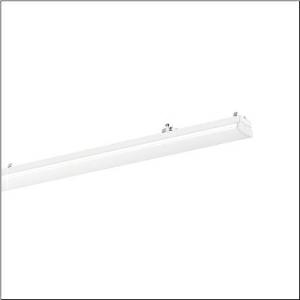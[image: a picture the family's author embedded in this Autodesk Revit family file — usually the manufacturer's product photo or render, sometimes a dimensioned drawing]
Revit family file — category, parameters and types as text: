
# Revit family: licross_r__11_recessed_opal_ho_51tl1dcn4cxm_8f08
name_source: partatom
category: Lighting Fixtures
units: mm (PartAtom-declared; Revit-internal decimal feet)

## family parameters
Cut with Voids When Loaded = No
Host = Face
Light Source = No
Part Type = Normal
Room Calculation Point = No
Round Connector Dimension = Use Diameter
Shared = No

## types (1)
- --- (1 x LED, 12370 lm, 66.5 W, 4000K)
    Apparent Load = 67 VA
    CIE Flux Codes = 44 73 91 87 100
    Color Rendering = 80
    Color Temperature = 4000K
    Default Elevation = 1800 mm
    Description = Licross® 11 recessed opal HO, luminaire insert, of sheet steel, coil coated, white, length: 1.500mm, width: 76mm, height: 87mm, LED rated luminous flux: 12.370lm, light colour: 840, control gear: ON/OFF Multilumen, CLOi, with plug, 3-pole, with phase selection, mains connection: 220..240V, AC, 50/60Hz, start of lifetime: 67W, end of service life: 75W, internal wiring halogen-free, primary optical cover: cover, of PMMA, light emission: direct with ceiling illumination distribution, primary light characteristic: symmetric, protection rating (complete): IP40, insulation class (complete): insulation class I (protective earthing), certification: CE, ENEC, VDE, UKCA, protection symbol: D if used in an environment without relevant dust loads with corresponding accessories, impact resistance: IK06, permissible ambient temperature for indoor applications: -35..+35°C, corresponds to IFS (International Featured Standards) requirements for safety and quality in the food industry, reducing of maximum allowable ambient temperature of 5°C with ceiling mounting, LABS conformity tested according to VDMA 24364:2018-05, packaging unit: 1 piece
    Height = 83 mm
    Lamp = 1 x LED
    Lamp Light Flux = 12370 lm
    Lamp Power = 66.5 W
    Lamp count = 1
    Length = 1500 mm
    Luminous efficacy = 186 lm/W
    Manufacturer = Siteco
    ModVariant = No
    Model = 51TL1DCN4CXM
    Mounting Place = Ceiling
    Mounting Type = Pendant
    Number of Poles = 1
    OnlyDefault = Yes
    Power Factor = 1
    Product Name = Licross® 11 recessed opal HO
    Product group = luminaire insert | ceiling pendant
    ProductGroupID = 902
    Protection Class = Protection class I
    Protection Degree = IP 40
    RLX_Detail_Level = 1
    RLX_Emergency_Light_Flux = 0 lm
    RLX_Emergency_Type = 0
    RLX_Emergency_Type_DB = No
    RlxData = <blob elided: 24941 chars, md5=9a208120>
    Socket = socket
    Standby Power = 0 W
    System Light Flux = 12370 lm
    System Power = 67 W
    Type Comments = factory setting: luminous flux: 100 % | (A | C | E) | 156 mA
    Type Image = l_1313666.jpg
    URL = http://relux.com
    VarID = @adj_089877
    Voltage = 0 V
    Weight = 0.00 kg
    Width = 76 mm

## geometry (parser evidence)
native form markers: Blend x4, Sweep x12
no freeform markers — native parametric forms only
